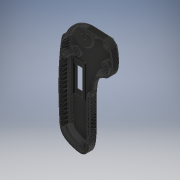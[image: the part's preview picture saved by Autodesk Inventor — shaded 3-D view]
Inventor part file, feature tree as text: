
AUTODESK INVENTOR PART (.ipt)
format: ipt  version: 2019.4 (Build 234330000, 330)  size: 9,392,128 bytes
history: native  units: mm
features: shell x1, other x1
ambient origin geometry x8: Origin, YZ Plane, XZ Plane, XY Plane, X Axis, Y Axis, Z Axis, Center Point
bodies: Solid1 (feature_tree)
feature tree (2):
  shell  "shell-top"  [1 undecoded]
  other  "MeshFeature1"
note: 1 required parameter value undecoded (feature->parameter linkage not recoverable at this tier; creation-order binding heuristic only, values carry confidence <= 0.55)
